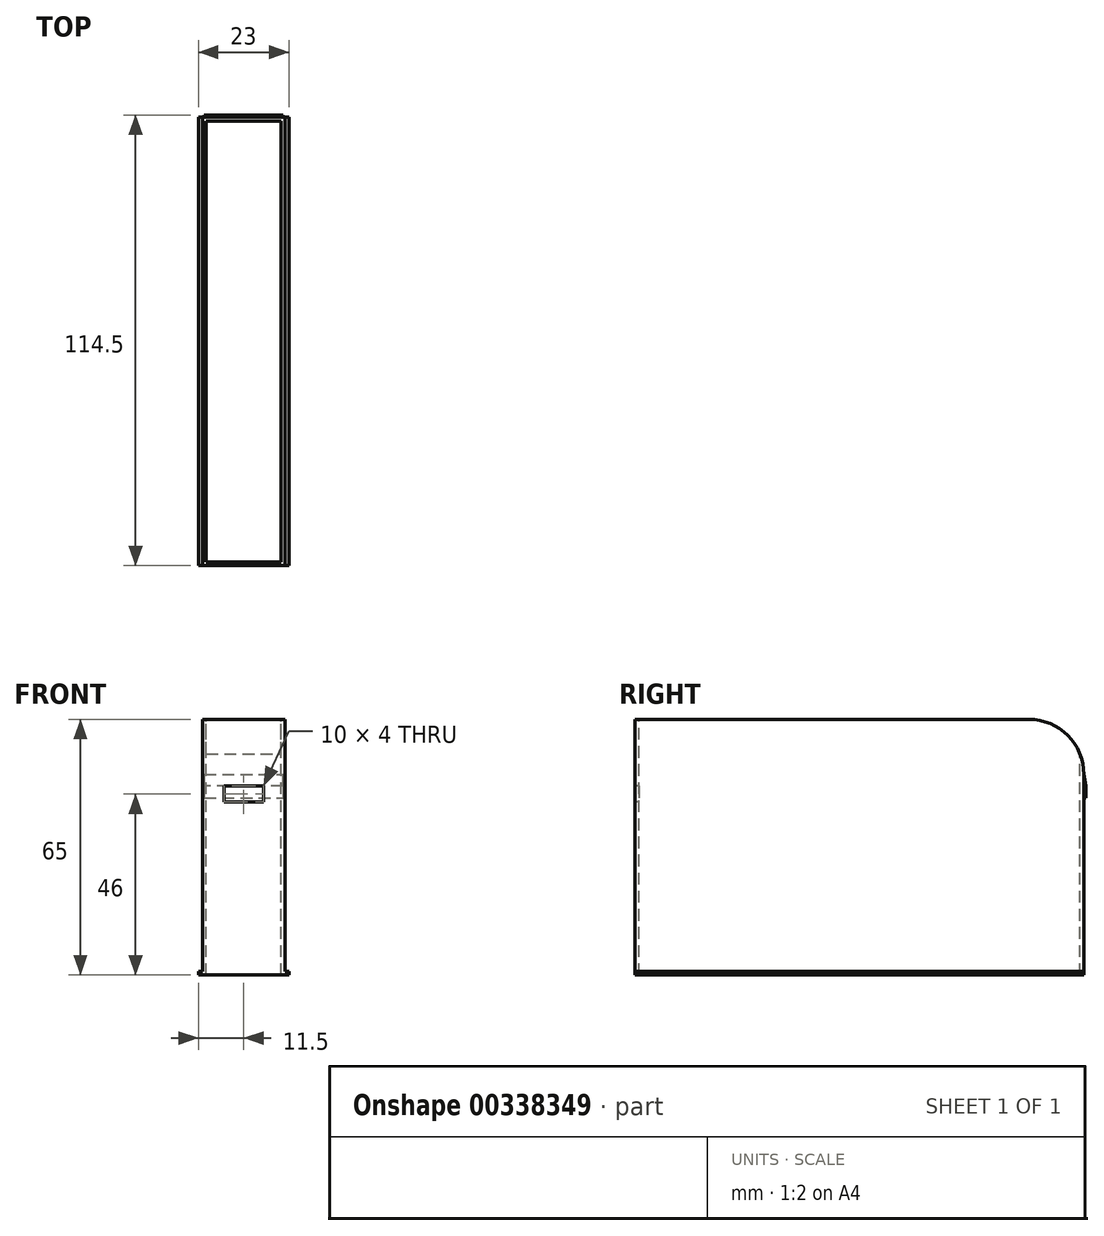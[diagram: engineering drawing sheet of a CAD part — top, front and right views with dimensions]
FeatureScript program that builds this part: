
annotation { "Feature Type Name" : "Feature", "Feature Type Description" : "" }
export const myFeature = defineFeature(function(context is Context, id is Id, definition is map)
    precondition{}
    {
        {
            var Q0;
            Q0=qCreatedBy(makeId("Top.planeOp"),FACE);
            var sketch = newSketch(context, id + "F0", { "sketchPlane" : qUnion([Q0])});
            skLineSegment(sketch, "E0.bottom", {"start": v(10.5, -57) * mm, "end": v(-10.5, -57) * mm});
            skLineSegment(sketch, "E0.top", {"start": v(10.5, 57) * mm, "end": v(-10.5, 57) * mm});
            skLineSegment(sketch, "E0.left", {"start": v(10.5, -57) * mm, "end": v(10.5, 57) * mm});
            skLineSegment(sketch, "E0.right", {"start": v(-10.5, -57) * mm, "end": v(-10.5, 57) * mm});
            skPoint(sketch, "E0.middle", {"position": v(0, 0) * mm});
            skSolve(sketch);
        }
        {
            var Q0;
            Q0 = qSketchRegion(id + "F0", true);
            extrude(context, id + "F1", {"entities" : qUnion([Q0]), "depth" : 65 * mm});
        }
        {
            var Q0;
            Q0=makeQuery(id+"F1.opExtrude","CAP_FACE",FACE,{"disambiguationData":[OSD([sQuery(id+"F0.wireOp",EDGE,"E0.bottom"),sQuery(id+"F0.wireOp",EDGE,"E0.top"),sQuery(id+"F0.wireOp",EDGE,"E0.left"),sQuery(id+"F0.wireOp",EDGE,"E0.right")])],"isStart":false});
            var sketch = newSketch(context, id + "F2", { "sketchPlane" : qUnion([Q0])});
            skLineSegment(sketch, "E1.bottom", {"start": v(9.5, -56) * mm, "end": v(-9.5, -56) * mm});
            skLineSegment(sketch, "E1.top", {"start": v(9.5, 56) * mm, "end": v(-9.5, 56) * mm});
            skLineSegment(sketch, "E1.left", {"start": v(9.5, -56) * mm, "end": v(9.5, 56) * mm});
            skLineSegment(sketch, "E1.right", {"start": v(-9.5, -56) * mm, "end": v(-9.5, 56) * mm});
            skPoint(sketch, "E1.middle", {"position": v(0, 0) * mm});
            skSolve(sketch);
        }
        {
            var Q0;
            Q0 = qSketchRegion(id + "F2", true);
            extrude(context, id + "F3", {"entities" : qUnion([Q0]), "operationType" : NewBodyOperationType.REMOVE, "oppositeDirection" : true, "depth" : 90 * mm});
        }
        {
            var Q0;
            Q0=makeQuery(id+"F1.opExtrude","SWEPT_FACE",FACE,{"disambiguationData":[OSD([sQuery(id+"F0.wireOp",EDGE,"E0.bottom")])]});
            var sketch = newSketch(context, id + "F4", { "sketchPlane" : qUnion([Q0])});
            skLineSegment(sketch, "E2.bottom", {"start": v(5, 44) * mm, "end": v(-5, 44) * mm});
            skLineSegment(sketch, "E2.top", {"start": v(5, 48) * mm, "end": v(-5, 48) * mm});
            skLineSegment(sketch, "E2.left", {"start": v(5, 44) * mm, "end": v(5, 48) * mm});
            skLineSegment(sketch, "E2.right", {"start": v(-5, 44) * mm, "end": v(-5, 48) * mm});
            skPoint(sketch, "E2.middle", {"position": v(0, 46) * mm});
            skSolve(sketch);
        }
        {
            var Q0;
            Q0 = qSketchRegion(id + "F4", true);
            extrude(context, id + "F5", {"entities" : qUnion([Q0]), "operationType" : NewBodyOperationType.REMOVE, "oppositeDirection" : true, "depth" : 25 * mm});
        }
        {
            var Q0;
            Q0=makeQuery(id+"F1.opExtrude","SWEPT_FACE",FACE,{"disambiguationData":[OSD([sQuery(id+"F0.wireOp",EDGE,"E0.left")])]});
            var sketch = newSketch(context, id + "F6", { "sketchPlane" : qUnion([Q0])});
            skLineSegment(sketch, "E3.bottom", {"start": v(-57, 0) * mm, "end": v(57, 0) * mm});
            skLineSegment(sketch, "E3.top", {"start": v(-57, 1) * mm, "end": v(57, 1) * mm});
            skLineSegment(sketch, "E3.left", {"start": v(-57, 0) * mm, "end": v(-57, 1) * mm});
            skLineSegment(sketch, "E3.right", {"start": v(57, 0) * mm, "end": v(57, 1) * mm});
            skSolve(sketch);
        }
        {
            var Q0;
            Q0 = qSketchRegion(id + "F6", true);
            extrude(context, id + "F7", {"entities" : qUnion([Q0]), "operationType" : NewBodyOperationType.ADD, "depth" : 1 * mm});
        }
        {
            var Q0;
            Q0=makeQuery(id+"F1.opExtrude","SWEPT_FACE",FACE,{"disambiguationData":[OSD([sQuery(id+"F0.wireOp",EDGE,"E0.right")])]});
            var sketch = newSketch(context, id + "F8", { "sketchPlane" : qUnion([Q0])});
            skLineSegment(sketch, "E4.bottom", {"start": v(57, 0) * mm, "end": v(-57, 0) * mm});
            skLineSegment(sketch, "E4.top", {"start": v(57, 1) * mm, "end": v(-57, 1) * mm});
            skLineSegment(sketch, "E4.left", {"start": v(57, 0) * mm, "end": v(57, 1) * mm});
            skLineSegment(sketch, "E4.right", {"start": v(-57, 0) * mm, "end": v(-57, 1) * mm});
            skSolve(sketch);
        }
        {
            var Q0;
            Q0 = qSketchRegion(id + "F8", true);
            extrude(context, id + "F9", {"entities" : qUnion([Q0]), "operationType" : NewBodyOperationType.ADD, "depth" : 1 * mm});
        }
        {
            var Q0;
            Q0=makeQuery(id+"F1.opExtrude","SWEPT_FACE",FACE,{"disambiguationData":[OSD([sQuery(id+"F0.wireOp",EDGE,"E0.left")])]});
            var sketch = newSketch(context, id + "F10", { "sketchPlane" : qUnion([Q0])});
            skArc(sketch, "E5", {"start": v(57, 51) * mm, "mid": v(52.9, 60.9) * mm, "end": v(43, 65) * mm});
            skSolve(sketch);
        }
        {
            var Q0;
            {var subQ0=sQuery(id+"F10.wireOp",EDGE,"E5");Q0=makeQuery(id+"F10.imprint","IMPRINT",FACE,{"disambiguationData":[TD([[makeQuery(id+"F10.imprint","IMPRINT",EDGE,{"derivedFrom":subQ0}),-1.0]])]});}
            extrude(context, id + "F11", {"entities" : qUnion([Q0]), "operationType" : NewBodyOperationType.REMOVE, "oppositeDirection" : true, "depth" : 25 * mm});
        }
        {
            var Q0;
            Q0=makeQuery(id+"F9.boolean.opBoolean","MERGE",FACE,{"derivedFrom":[makeQuery(id+"F7.boolean.opBoolean","MERGE",FACE,{"derivedFrom":[makeQuery(id+"F1.opExtrude","SWEPT_FACE",FACE,{"disambiguationData":[OSD([sQuery(id+"F0.wireOp",EDGE,"E0.top")])]}),makeQuery(id+"F7.opExtrude","SWEPT_FACE",FACE,{"disambiguationData":[OSD([sQuery(id+"F6.wireOp",EDGE,"E3.right")])]})]}),makeQuery(id+"F9.opExtrude","SWEPT_FACE",FACE,{"disambiguationData":[OSD([sQuery(id+"F8.wireOp",EDGE,"E4.right")])]})]});
            var sketch = newSketch(context, id + "F12", { "sketchPlane" : qUnion([Q0])});
            skLineSegment(sketch, "E6.bottom", {"start": v(10, 56.2) * mm, "end": v(-10, 56.2) * mm});
            skLineSegment(sketch, "E6.top", {"start": v(10, 45) * mm, "end": v(-10, 45) * mm});
            skLineSegment(sketch, "E6.left", {"start": v(10, 56.2) * mm, "end": v(10, 45) * mm});
            skLineSegment(sketch, "E6.right", {"start": v(-10, 56.2) * mm, "end": v(-10, 45) * mm});
            skSolve(sketch);
        }
        {
            var Q0;
            {var subQ0=sQuery(id+"F12.wireOp",EDGE,"E6.top");Q0=makeQuery(id+"F12.imprint","IMPRINT",FACE,{"disambiguationData":[TD([[makeQuery(id+"F12.imprint","IMPRINT",EDGE,{"derivedFrom":subQ0}),-1.0]])]});}
            extrude(context, id + "F13", {"entities" : qUnion([Q0]), "operationType" : NewBodyOperationType.ADD, "depth" : 0.5 * mm});
        }
        {
            var Q0;
            Q0=makeQuery(id+"F13.opExtrude","SWEPT_FACE",FACE,{"disambiguationData":[OSD([sQuery(id+"F12.wireOp",EDGE,"E6.left")])]});
            var sketch = newSketch(context, id + "F14", { "sketchPlane" : qUnion([Q0])});
            skLineSegment(sketch, "E7", {"start": v(-57.5, 48) * mm, "end": v(-57, 51) * mm});
            skSolve(sketch);
        }
        {
            var Q0;
            {var subQ0=sQuery(id+"F14.wireOp",EDGE,"E7");Q0=makeQuery(id+"F14.imprint","IMPRINT",FACE,{"disambiguationData":[TD([[makeQuery(id+"F14.imprint","IMPRINT",EDGE,{"derivedFrom":subQ0}),1.0]])]});}
            extrude(context, id + "F15", {"entities" : qUnion([Q0]), "operationType" : NewBodyOperationType.REMOVE, "oppositeDirection" : true, "depth" : 25 * mm});
        }
    });
